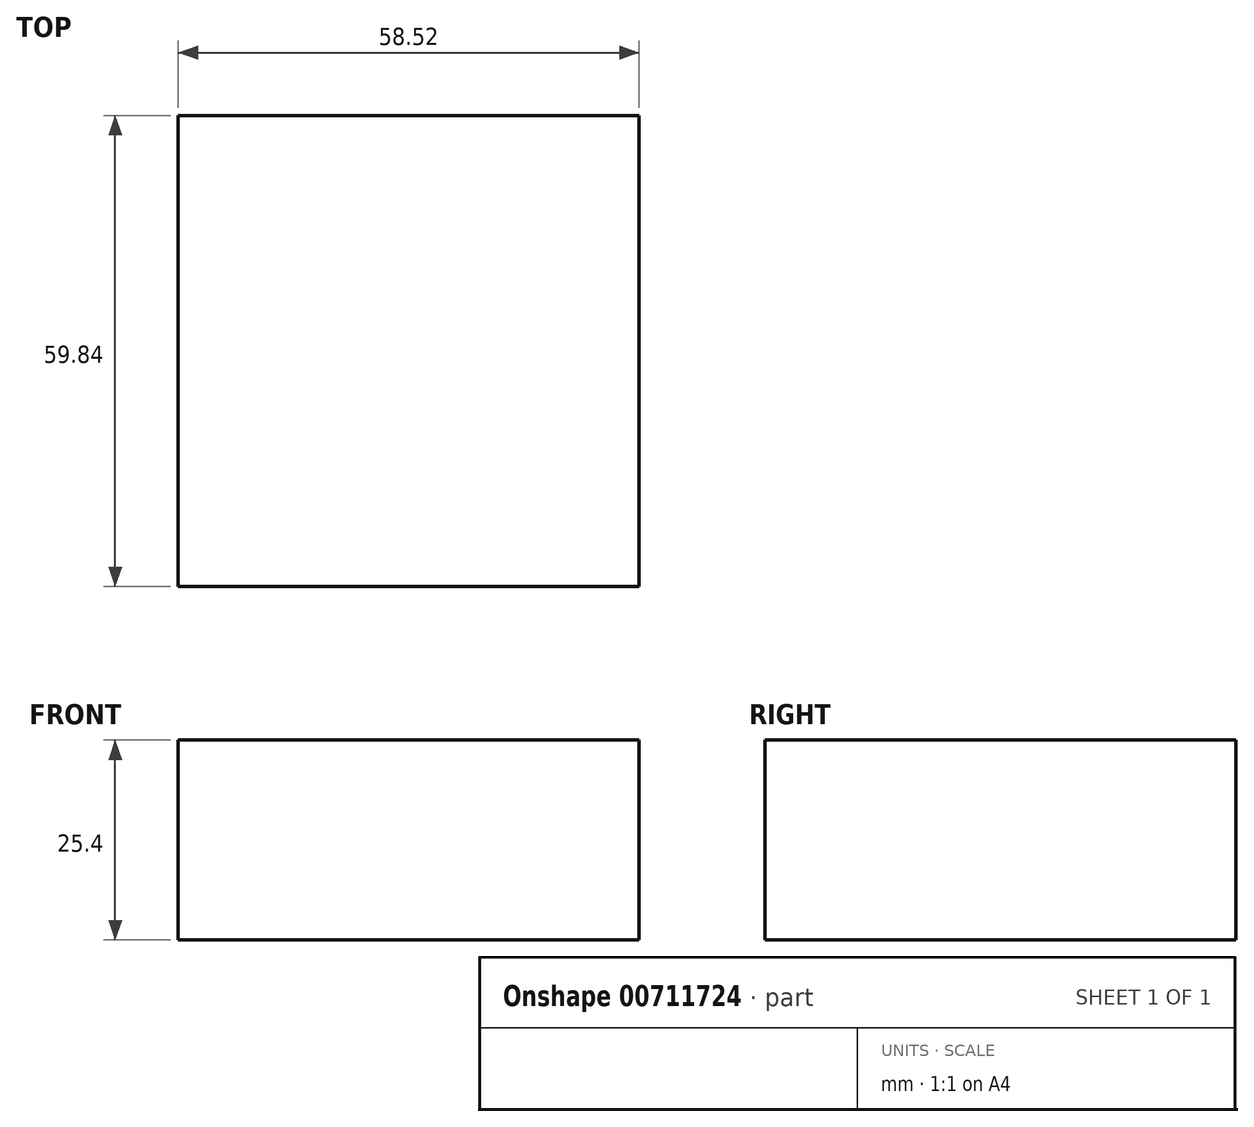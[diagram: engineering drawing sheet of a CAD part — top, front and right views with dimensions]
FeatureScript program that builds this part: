
annotation { "Feature Type Name" : "Feature", "Feature Type Description" : "" }
export const myFeature = defineFeature(function(context is Context, id is Id, definition is map)
    precondition{}
    {
        {
            var Q0;
            Q0=qCreatedBy(makeId("Top.planeOp"),FACE);
            var sketch = newSketch(context, id + "F0", { "sketchPlane" : qUnion([Q0])});
            skLineSegment(sketch, "E0.bottom", {"start": v(29.26, -29.92) * mm, "end": v(-29.26, -29.92) * mm});
            skLineSegment(sketch, "E0.top", {"start": v(29.26, 29.92) * mm, "end": v(-29.26, 29.92) * mm});
            skLineSegment(sketch, "E0.left", {"start": v(29.26, -29.92) * mm, "end": v(29.26, 29.92) * mm});
            skLineSegment(sketch, "E0.right", {"start": v(-29.26, -29.92) * mm, "end": v(-29.26, 29.92) * mm});
            skPoint(sketch, "E0.middle", {"position": v(0, 0) * mm});
            skSolve(sketch);
        }
        {
            var Q0;
            Q0=makeQuery(id+"F0.imprint","IMPRINT",FACE,{"disambiguationData":[TD([[makeQuery(id+"F0.imprint","IMPRINT",EDGE,{"derivedFrom":sQuery(id+"F0.wireOp",EDGE,"E0.bottom")}),-1.0]])]});
            extrude(context, id + "F1", {"entities" : qUnion([Q0]), "depth" : 25.4 * mm, "offsetDistance" : 25.4 * mm});
        }
    });
